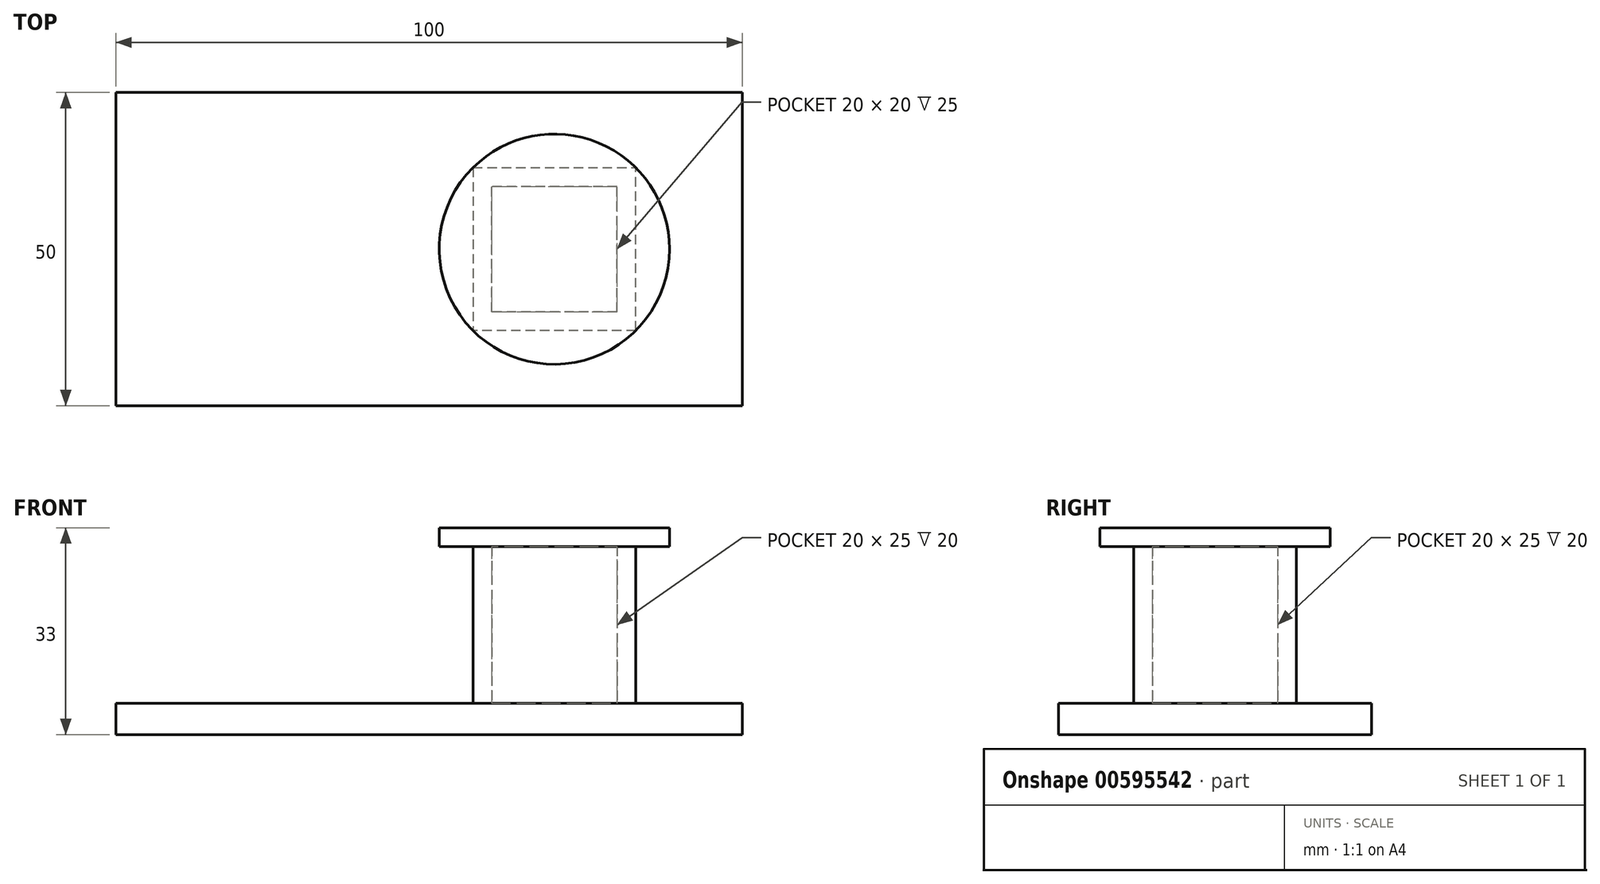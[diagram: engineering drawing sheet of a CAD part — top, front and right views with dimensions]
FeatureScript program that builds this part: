
annotation { "Feature Type Name" : "Feature", "Feature Type Description" : "" }
export const myFeature = defineFeature(function(context is Context, id is Id, definition is map)
    precondition{}
    {
        {
            var Q0;
            Q0=qCreatedBy(makeId("Top.planeOp"),FACE);
            var sketch = newSketch(context, id + "F0", { "sketchPlane" : qUnion([Q0])});
            skLineSegment(sketch, "E0.bottom", {"start": v(-50, -25) * mm, "end": v(50, -25) * mm});
            skLineSegment(sketch, "E0.top", {"start": v(-50, 25) * mm, "end": v(50, 25) * mm});
            skLineSegment(sketch, "E0.left", {"start": v(-50, -25) * mm, "end": v(-50, 25) * mm});
            skLineSegment(sketch, "E0.right", {"start": v(50, -25) * mm, "end": v(50, 25) * mm});
            skPoint(sketch, "E0.middle", {"position": v(0, 0) * mm});
            skLineSegment(sketch, "E1", {"start": v(10, 25) * mm, "end": v(10, -25) * mm});
            skLineSegment(sketch, "E2", {"start": v(10, 10) * mm, "end": v(50, 10) * mm});
            skLineSegment(sketch, "E3", {"start": v(10, -10) * mm, "end": v(50, -10) * mm});
            skLineSegment(sketch, "E4", {"start": v(30, 10) * mm, "end": v(30, -10) * mm});
            skLineSegment(sketch, "E5", {"start": v(30, 10) * mm, "end": v(30, 25) * mm});
            skLineSegment(sketch, "E6", {"start": v(30, -10) * mm, "end": v(30, -25) * mm});
            skLineSegment(sketch, "E7", {"start": v(30, -13) * mm, "end": v(10, -13) * mm});
            skLineSegment(sketch, "E8", {"start": v(30, 13) * mm, "end": v(10, 13) * mm});
            skLineSegment(sketch, "E9", {"start": v(30, 13) * mm, "end": v(50, 13) * mm});
            skLineSegment(sketch, "E10", {"start": v(30, -13) * mm, "end": v(50, -13) * mm});
            skLineSegment(sketch, "E11", {"start": v(33, 13) * mm, "end": v(33, -13) * mm});
            skLineSegment(sketch, "E12", {"start": v(-3.89, 25) * mm, "end": v(-3.89, -25) * mm});
            skLineSegment(sketch, "E13", {"start": v(10, 13) * mm, "end": v(-3.89, 13) * mm});
            skLineSegment(sketch, "E14", {"start": v(10, -13) * mm, "end": v(-3.89, -13) * mm});
            skLineSegment(sketch, "E15", {"start": v(7, -13) * mm, "end": v(7, 13) * mm});
            skSolve(sketch);
        }
        {
            var Q0;
            Q0=makeQuery(id+"F0.imprint","IMPRINT",FACE,{"disambiguationData":[TD([[makeQuery(id+"F0.imprint","IMPRINT",EDGE,{"derivedFrom":sQuery(id+"F0.wireOp",EDGE,"E0.bottom")}),1.0]])]});
            var Q1;
            {var subQ0=sQuery(id+"F0.wireOp",EDGE,"E4gdXj6o-lhgj-VyLo-uplc-6VLiuRCqNSEE");Q1=makeQuery(id+"F0.imprint","IMPRINT",FACE,{"disambiguationData":[TD([[makeQuery(id+"F0.imprint","IMPRINT",EDGE,{"derivedFrom":subQ0}),-1.0]])]});}
            var Q2;
            {var subQ5=sQuery(id+"F0.wireOp",EDGE,"E4gdXj6o-lhgj-VyLo-uplc-6VLiuRCqNSEE");Q2=makeQuery(id+"F0.imprint","IMPRINT",FACE,{"disambiguationData":[TD([[makeQuery(id+"F0.imprint","IMPRINT",EDGE,{"derivedFrom":subQ5}),1.0]])]});}
            var Q3;
            {var subQ4=sQuery(id+"F0.wireOp",EDGE,"E0.left");Q3=makeQuery(id+"F0.imprint","IMPRINT",FACE,{"disambiguationData":[TD([[makeQuery(id+"F0.imprint","IMPRINT",EDGE,{"derivedFrom":subQ4}),-1.0]])]});}
            var Q4;
            {var subQ4=sQuery(id+"F0.wireOp",EDGE,"E0.right");var subQ5=sQuery(id+"F0.wireOp",EDGE,"E0.top");var subQ6=makeQuery(id+"F0.imprint","INTERSECT",VERTEX,{"derivedFrom":[subQ5,subQ4]});Q4=makeQuery(id+"F0.imprint","IMPRINT",FACE,{"disambiguationData":[TD([[makeQuery(id+"F0.imprint","IMPRINT",EDGE,{"disambiguationData":[TD([[subQ6,1.0]])],"derivedFrom":subQ5}),-1.0]])]});}
            var Q5;
            {var subQ0=sQuery(id+"F0.wireOp",EDGE,"E2");var subQ1=sQuery(id+"F0.wireOp",EDGE,"E1");var subQ2=makeQuery(id+"F0.imprint","INTERSECT",VERTEX,{"derivedFrom":[subQ1,subQ0]});Q5=makeQuery(id+"F0.imprint","IMPRINT",FACE,{"disambiguationData":[TD([[makeQuery(id+"F0.imprint","IMPRINT",EDGE,{"disambiguationData":[TD([[subQ2,-1.0]])],"derivedFrom":subQ1}),1.0]])]});}
            var Q6;
            {var subQ0=sQuery(id+"F0.wireOp",EDGE,"E2");var subQ1=sQuery(id+"F0.wireOp",EDGE,"E0.right");var subQ2=makeQuery(id+"F0.imprint","INTERSECT",VERTEX,{"derivedFrom":[subQ1,subQ0]});Q6=makeQuery(id+"F0.imprint","IMPRINT",FACE,{"disambiguationData":[TD([[makeQuery(id+"F0.imprint","IMPRINT",EDGE,{"disambiguationData":[TD([[subQ2,1.0]])],"derivedFrom":subQ1}),1.0]])]});}
            var Q7;
            {var subQ5=sQuery(id+"F0.wireOp",EDGE,"E8");Q7=makeQuery(id+"F0.imprint","IMPRINT",FACE,{"disambiguationData":[TD([[makeQuery(id+"F0.imprint","IMPRINT",EDGE,{"derivedFrom":subQ5}),-1.0]])]});}
            var Q8;
            {var subQ3=sQuery(id+"F0.wireOp",EDGE,"E8");Q8=makeQuery(id+"F0.imprint","IMPRINT",FACE,{"disambiguationData":[TD([[makeQuery(id+"F0.imprint","IMPRINT",EDGE,{"derivedFrom":subQ3}),1.0]])]});}
            var Q9;
            {var subQ3=sQuery(id+"F0.wireOp",EDGE,"E11");var subQ5=sQuery(id+"F0.wireOp",EDGE,"E9");var subQ7=makeQuery(id+"F0.imprint","INTERSECT",VERTEX,{"derivedFrom":[subQ5,subQ3]});Q9=makeQuery(id+"F0.imprint","IMPRINT",FACE,{"disambiguationData":[TD([[makeQuery(id+"F0.imprint","IMPRINT",EDGE,{"disambiguationData":[TD([[subQ7,-1.0]])],"derivedFrom":subQ3}),-1.0]])]});}
            var Q10;
            {var subQ0=sQuery(id+"F0.wireOp",EDGE,"E2");var subQ1=sQuery(id+"F0.wireOp",EDGE,"E0.right");var subQ2=makeQuery(id+"F0.imprint","INTERSECT",VERTEX,{"derivedFrom":[subQ1,subQ0]});Q10=makeQuery(id+"F0.imprint","IMPRINT",FACE,{"disambiguationData":[TD([[makeQuery(id+"F0.imprint","IMPRINT",EDGE,{"disambiguationData":[TD([[subQ2,-1.0]])],"derivedFrom":subQ1}),1.0]])]});}
            var Q11;
            {var subQ0=sQuery(id+"F0.wireOp",EDGE,"E4");Q11=makeQuery(id+"F0.imprint","IMPRINT",FACE,{"disambiguationData":[TD([[makeQuery(id+"F0.imprint","IMPRINT",EDGE,{"derivedFrom":subQ0}),1.0]])]});}
            var Q12;
            {var subQ0=sQuery(id+"F0.wireOp",EDGE,"E3");var subQ1=sQuery(id+"F0.wireOp",EDGE,"E0.right");var subQ2=makeQuery(id+"F0.imprint","INTERSECT",VERTEX,{"derivedFrom":[subQ1,subQ0]});Q12=makeQuery(id+"F0.imprint","IMPRINT",FACE,{"disambiguationData":[TD([[makeQuery(id+"F0.imprint","IMPRINT",EDGE,{"disambiguationData":[TD([[subQ2,1.0]])],"derivedFrom":subQ1}),1.0]])]});}
            var Q13;
            {var subQ4=sQuery(id+"F0.wireOp",EDGE,"E0.bottom");var subQ6=sQuery(id+"F0.wireOp",EDGE,"E0.right");var subQ7=makeQuery(id+"F0.imprint","INTERSECT",VERTEX,{"derivedFrom":[subQ4,subQ6]});Q13=makeQuery(id+"F0.imprint","IMPRINT",FACE,{"disambiguationData":[TD([[makeQuery(id+"F0.imprint","IMPRINT",EDGE,{"disambiguationData":[TD([[subQ7,1.0]])],"derivedFrom":subQ4}),1.0]])]});}
            var Q14;
            {var subQ3=sQuery(id+"F0.wireOp",EDGE,"E11");var subQ5=sQuery(id+"F0.wireOp",EDGE,"E10");var subQ7=makeQuery(id+"F0.imprint","INTERSECT",VERTEX,{"derivedFrom":[subQ5,subQ3]});Q14=makeQuery(id+"F0.imprint","IMPRINT",FACE,{"disambiguationData":[TD([[makeQuery(id+"F0.imprint","IMPRINT",EDGE,{"disambiguationData":[TD([[subQ7,1.0]])],"derivedFrom":subQ3}),-1.0]])]});}
            var Q15;
            {var subQ3=sQuery(id+"F0.wireOp",EDGE,"E7");Q15=makeQuery(id+"F0.imprint","IMPRINT",FACE,{"disambiguationData":[TD([[makeQuery(id+"F0.imprint","IMPRINT",EDGE,{"derivedFrom":subQ3}),-1.0]])]});}
            var Q16;
            {var subQ1=sQuery(id+"F0.wireOp",EDGE,"E1");var subQ4=sQuery(id+"F0.wireOp",EDGE,"E0.bottom");var subQ5=makeQuery(id+"F0.imprint","INTERSECT",VERTEX,{"derivedFrom":[subQ4,subQ1]});Q16=makeQuery(id+"F0.imprint","IMPRINT",FACE,{"disambiguationData":[TD([[makeQuery(id+"F0.imprint","IMPRINT",EDGE,{"disambiguationData":[TD([[subQ5,1.0]])],"derivedFrom":subQ4}),1.0]])]});}
            var Q17;
            {var subQ5=sQuery(id+"F0.wireOp",EDGE,"E15");Q17=makeQuery(id+"F0.imprint","IMPRINT",FACE,{"disambiguationData":[TD([[makeQuery(id+"F0.imprint","IMPRINT",EDGE,{"derivedFrom":subQ5}),1.0]])]});}
            var Q18;
            {var subQ1=sQuery(id+"F0.wireOp",EDGE,"E1");var subQ5=sQuery(id+"F0.wireOp",EDGE,"E0.top");var subQ8=makeQuery(id+"F0.imprint","INTERSECT",VERTEX,{"derivedFrom":[subQ5,subQ1]});Q18=makeQuery(id+"F0.imprint","IMPRINT",FACE,{"disambiguationData":[TD([[makeQuery(id+"F0.imprint","IMPRINT",EDGE,{"disambiguationData":[TD([[subQ8,1.0]])],"derivedFrom":subQ5}),-1.0]])]});}
            var Q19;
            {var subQ3=sQuery(id+"F0.wireOp",EDGE,"E15");Q19=makeQuery(id+"F0.imprint","IMPRINT",FACE,{"disambiguationData":[TD([[makeQuery(id+"F0.imprint","IMPRINT",EDGE,{"derivedFrom":subQ3}),-1.0]])]});}
            extrude(context, id + "F1", {"entities" : qUnion([Q0, Q1, Q2, Q3, Q4, Q5, Q6, Q7, Q8, Q9, Q10, Q11, Q12, Q13, Q14, Q15, Q16, Q17, Q18, Q19]), "depth" : 5 * mm, "offsetDistance" : 25 * mm});
        }
        {
            var Q0;
            {var subQ3=sQuery(id+"F0.wireOp",EDGE,"E8");Q0=makeQuery(id+"F0.imprint","IMPRINT",FACE,{"disambiguationData":[TD([[makeQuery(id+"F0.imprint","IMPRINT",EDGE,{"derivedFrom":subQ3}),1.0]])]});}
            var Q1;
            {var subQ3=sQuery(id+"F0.wireOp",EDGE,"E11");var subQ5=sQuery(id+"F0.wireOp",EDGE,"E9");var subQ7=makeQuery(id+"F0.imprint","INTERSECT",VERTEX,{"derivedFrom":[subQ5,subQ3]});Q1=makeQuery(id+"F0.imprint","IMPRINT",FACE,{"disambiguationData":[TD([[makeQuery(id+"F0.imprint","IMPRINT",EDGE,{"disambiguationData":[TD([[subQ7,-1.0]])],"derivedFrom":subQ3}),-1.0]])]});}
            var Q2;
            {var subQ0=sQuery(id+"F0.wireOp",EDGE,"E4");Q2=makeQuery(id+"F0.imprint","IMPRINT",FACE,{"disambiguationData":[TD([[makeQuery(id+"F0.imprint","IMPRINT",EDGE,{"derivedFrom":subQ0}),1.0]])]});}
            var Q3;
            {var subQ3=sQuery(id+"F0.wireOp",EDGE,"E11");var subQ5=sQuery(id+"F0.wireOp",EDGE,"E10");var subQ7=makeQuery(id+"F0.imprint","INTERSECT",VERTEX,{"derivedFrom":[subQ5,subQ3]});Q3=makeQuery(id+"F0.imprint","IMPRINT",FACE,{"disambiguationData":[TD([[makeQuery(id+"F0.imprint","IMPRINT",EDGE,{"disambiguationData":[TD([[subQ7,1.0]])],"derivedFrom":subQ3}),-1.0]])]});}
            var Q4;
            {var subQ3=sQuery(id+"F0.wireOp",EDGE,"E7");Q4=makeQuery(id+"F0.imprint","IMPRINT",FACE,{"disambiguationData":[TD([[makeQuery(id+"F0.imprint","IMPRINT",EDGE,{"derivedFrom":subQ3}),-1.0]])]});}
            var Q5;
            {var subQ3=sQuery(id+"F0.wireOp",EDGE,"E15");Q5=makeQuery(id+"F0.imprint","IMPRINT",FACE,{"disambiguationData":[TD([[makeQuery(id+"F0.imprint","IMPRINT",EDGE,{"derivedFrom":subQ3}),-1.0]])]});}
            extrude(context, id + "F2", {"entities" : qUnion([Q0, Q1, Q2, Q3, Q4, Q5]), "operationType" : NewBodyOperationType.ADD, "depth" : 30 * mm, "offsetDistance" : 25 * mm});
        }
        {
            var Q0;
            Q0=makeQuery(id+"F2.opExtrude","CAP_FACE",FACE,{"disambiguationData":[OSD([sQuery(id+"F0.wireOp",EDGE,"E1"),sQuery(id+"F0.wireOp",EDGE,"E2"),sQuery(id+"F0.wireOp",EDGE,"E3"),sQuery(id+"F0.wireOp",EDGE,"E4"),sQuery(id+"F0.wireOp",EDGE,"E7"),sQuery(id+"F0.wireOp",EDGE,"E8"),sQuery(id+"F0.wireOp",EDGE,"E9"),sQuery(id+"F0.wireOp",EDGE,"E10"),sQuery(id+"F0.wireOp",EDGE,"E11"),sQuery(id+"F0.wireOp",EDGE,"E13"),sQuery(id+"F0.wireOp",EDGE,"E14"),sQuery(id+"F0.wireOp",EDGE,"E15")])],"isStart":false});
            var sketch = newSketch(context, id + "F3", { "sketchPlane" : qUnion([Q0])});
            skLineSegment(sketch, "E16", {"start": v(33, 13) * mm, "end": v(7, -13) * mm});
            skLineSegment(sketch, "E17", {"start": v(7, -13) * mm, "end": v(7, 13) * mm});
            skLineSegment(sketch, "E18", {"start": v(7, 13) * mm, "end": v(33, -13) * mm});
            skCircle(sketch, "E19", {"center": v(20, 0) * mm, "radius": 18.38 * mm});
            skSolve(sketch);
        }
        {
            var Q0;
            Q0 = qSketchRegion(id + "F3", true);
            extrude(context, id + "F4", {"entities" : qUnion([Q0]), "operationType" : NewBodyOperationType.ADD, "depth" : 3 * mm, "offsetDistance" : 25 * mm});
        }
    });
